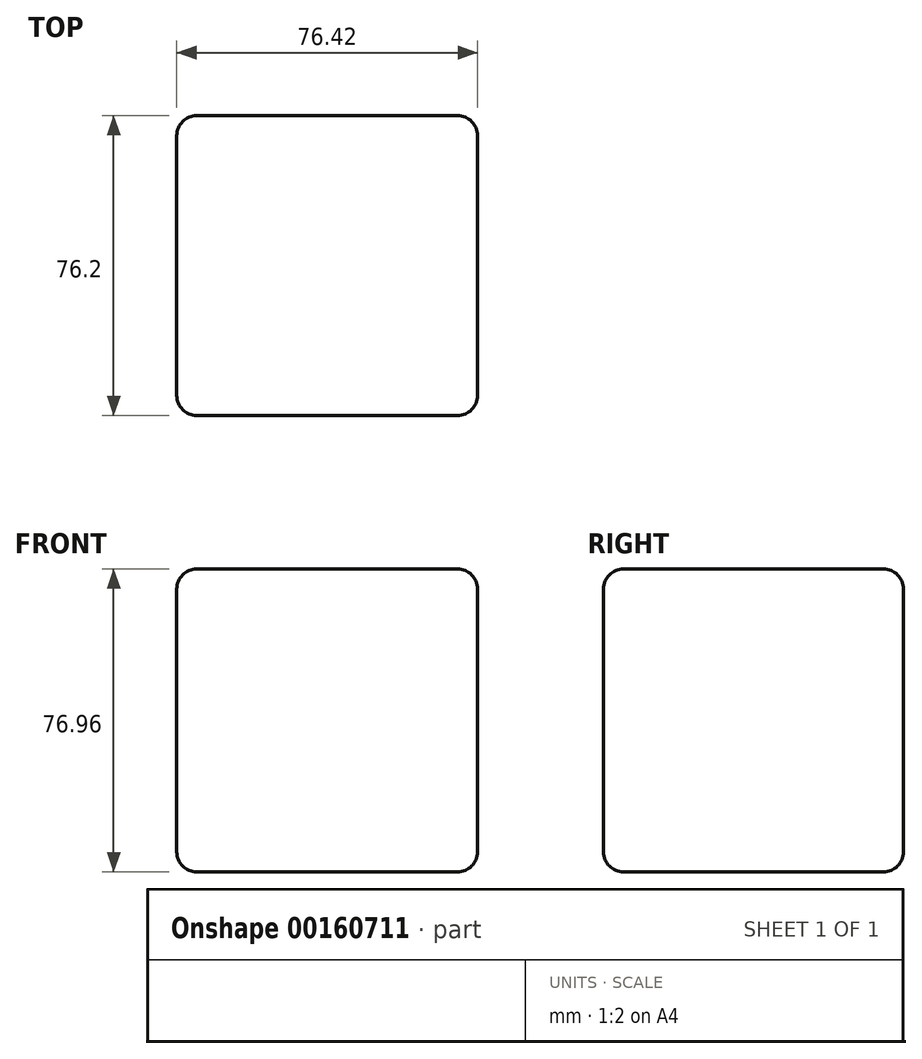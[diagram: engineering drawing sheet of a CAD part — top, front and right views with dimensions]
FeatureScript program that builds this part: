
annotation { "Feature Type Name" : "Feature", "Feature Type Description" : "" }
export const myFeature = defineFeature(function(context is Context, id is Id, definition is map)
    precondition{}
    {
        {
            var Q0;
            Q0=qCreatedBy(makeId("Front.planeOp"),FACE);
            var sketch = newSketch(context, id + "F0", { "sketchPlane" : qUnion([Q0])});
            skLineSegment(sketch, "E0.bottom", {"start": v(-38.2, 38.48) * mm, "end": v(38.2, 38.48) * mm});
            skLineSegment(sketch, "E0.top", {"start": v(-38.2, -38.48) * mm, "end": v(38.2, -38.48) * mm});
            skLineSegment(sketch, "E0.left", {"start": v(-38.2, 38.48) * mm, "end": v(-38.2, -38.48) * mm});
            skLineSegment(sketch, "E0.right", {"start": v(38.2, 38.48) * mm, "end": v(38.2, -38.48) * mm});
            skPoint(sketch, "E0.middle", {"position": v(0, 0) * mm});
            skSolve(sketch);
        }
        {
            var Q0;
            Q0 = qSketchRegion(id + "F0", true);
            extrude(context, id + "F1", {"entities" : qUnion([Q0]), "depth" : 38.1 * mm, "hasSecondDirection" : true, "secondDirectionOppositeDirection" : true, "secondDirectionDepth" : 38.1 * mm});
        }
        {
            var Q0;
            Q0=makeQuery(id+"F1.opExtrude","SWEPT_EDGE",EDGE,{"disambiguationData":[OSD([sQuery(id+"F0.wireOp",EDGE,"E0.bottom"),sQuery(id+"F0.wireOp",EDGE,"E0.right")])]});
            var Q1;
            Q1=makeQuery(id+"F1.opExtrude","CAP_EDGE",EDGE,{"disambiguationData":[OSD([sQuery(id+"F0.wireOp",EDGE,"E0.bottom")])],"isStart":true});
            var Q2;
            Q2=makeQuery(id+"F1.opExtrude","CAP_EDGE",EDGE,{"disambiguationData":[OSD([sQuery(id+"F0.wireOp",EDGE,"E0.right")])],"isStart":true});
            var Q3;
            Q3=makeQuery(id+"F1.opExtrude","SWEPT_EDGE",EDGE,{"disambiguationData":[OSD([sQuery(id+"F0.wireOp",EDGE,"E0.top"),sQuery(id+"F0.wireOp",EDGE,"E0.right")])]});
            var Q4;
            Q4=makeQuery(id+"F1.opExtrude","CAP_FACE",FACE,{"disambiguationData":[OSD([sQuery(id+"F0.wireOp",EDGE,"E0.bottom"),sQuery(id+"F0.wireOp",EDGE,"E0.top"),sQuery(id+"F0.wireOp",EDGE,"E0.left"),sQuery(id+"F0.wireOp",EDGE,"E0.right")])],"isStart":true});
            var Q5;
            Q5=makeQuery(id+"F1.opExtrude","CAP_FACE",FACE,{"disambiguationData":[OSD([sQuery(id+"F0.wireOp",EDGE,"E0.bottom"),sQuery(id+"F0.wireOp",EDGE,"E0.top"),sQuery(id+"F0.wireOp",EDGE,"E0.left"),sQuery(id+"F0.wireOp",EDGE,"E0.right")])],"isStart":false});
            var Q6;
            Q6=makeQuery(id+"F1.opExtrude","SWEPT_FACE",FACE,{"disambiguationData":[OSD([sQuery(id+"F0.wireOp",EDGE,"E0.left")])]});
            fillet(context, id + "F2", {"entities" : qUnion([Q0, Q1, Q2, Q3, Q4, Q5, Q6]), "radius" : 5.08 * mm, "tangentPropagation" : true, "allowEdgeOverflow" : false});
        }
    });
